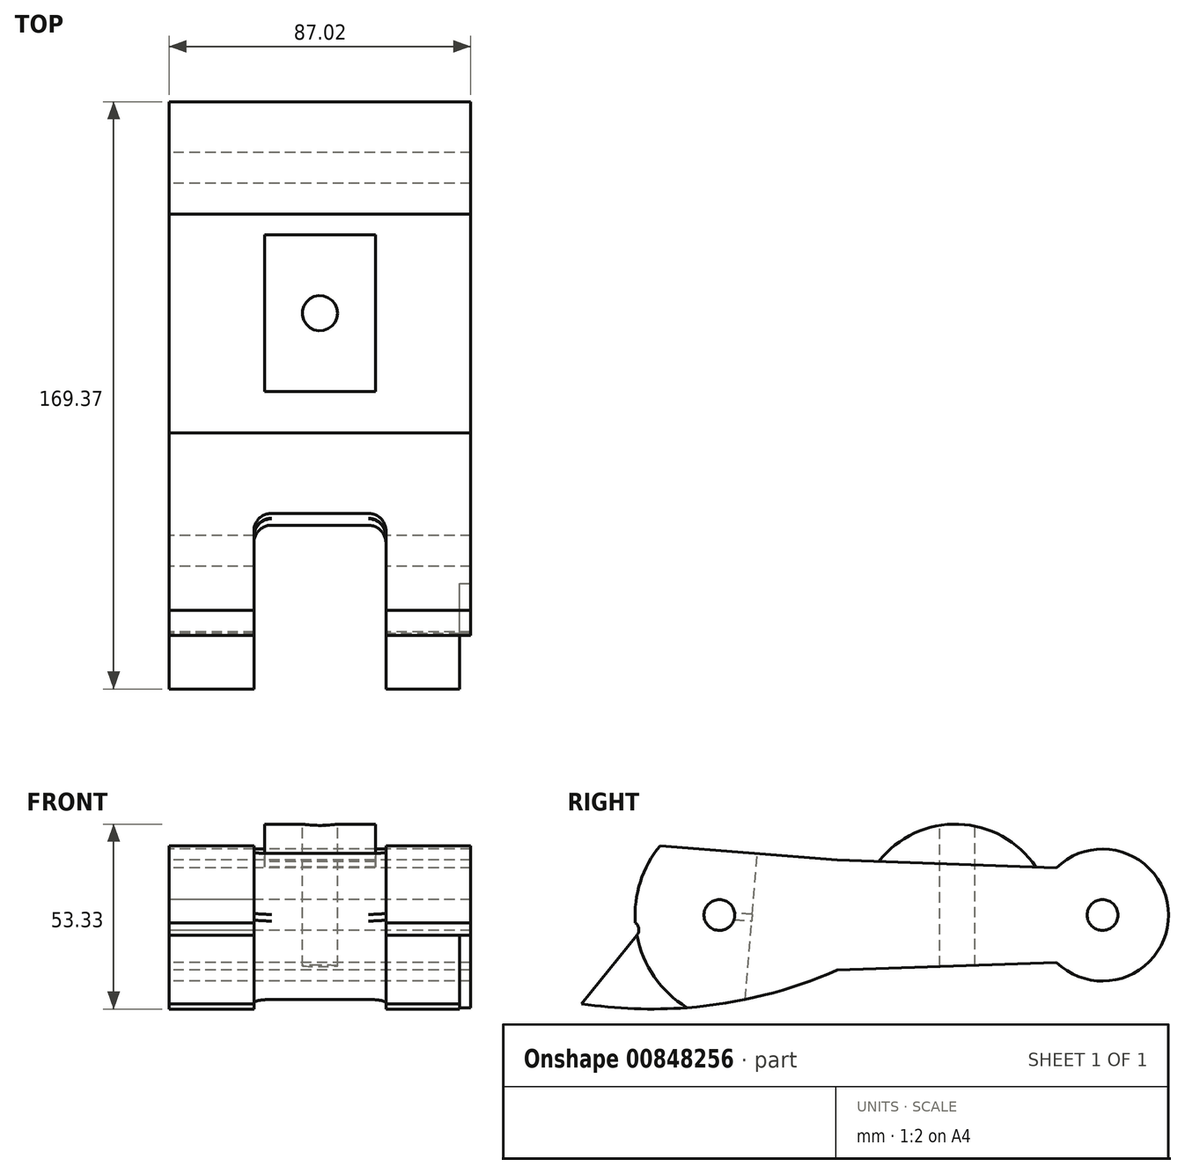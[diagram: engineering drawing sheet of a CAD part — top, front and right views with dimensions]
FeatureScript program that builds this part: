
annotation { "Feature Type Name" : "Feature", "Feature Type Description" : "" }
export const myFeature = defineFeature(function(context is Context, id is Id, definition is map)
    precondition{}
    {
        {
            var Q0;
            Q0=qCreatedBy(makeId("Right.planeOp"),FACE);
            var sketch = newSketch(context, id + "F0", { "sketchPlane" : qUnion([Q0])});
            skArc(sketch, "E0", {"start": v(43.17, -13.65) * mm, "mid": v(75.5, 0) * mm, "end": v(43.17, 13.65) * mm});
            skLineSegment(sketch, "E1", {"start": v(-105.47, 0) * mm, "end": v(-105.47, 71.25) * mm, "construction": true});
            skLineSegment(sketch, "E2", {"start": v(75.5, 0) * mm, "end": v(75.5, 75.21) * mm, "construction": true});
            skLineSegment(sketch, "E3", {"start": v(37.4, 0) * mm, "end": v(37.4, 13.65) * mm, "construction": true});
            skCircle(sketch, "E4", {"center": v(56.46, 0) * mm, "radius": 4.45 * mm});
            skCircle(sketch, "E5", {"center": v(-54.09, 0) * mm, "radius": 4.45 * mm});
            skLineSegment(sketch, "E6", {"start": v(-47.08, -35.85) * mm, "end": v(-47.08, 32.52) * mm, "construction": true});
            skArc(sketch, "E7", {"start": v(-20.04, -15.86) * mm, "mid": v(-15.73, 0) * mm, "end": v(-20.04, 15.86) * mm});
            skPoint(sketch, "E7.centerSnap0", {"position": v(-47.08, -1.67) * mm});
            skLineSegment(sketch, "E8.trimOffspring", {"start": v(-20.04, -15.86) * mm, "end": v(43.17, -13.65) * mm});
            skLineSegment(sketch, "E9.trimOffspring", {"start": v(-20.04, 15.86) * mm, "end": v(43.17, 13.65) * mm});
            skCircle(sketch, "E10", {"center": v(-47.08, 0) * mm, "radius": 31.98 * mm, "construction": true});
            skLineSegment(sketch, "E11", {"start": v(-71.2, 21) * mm, "end": v(-71.2, -21) * mm, "construction": true});
            skLineSegment(sketch, "E12", {"start": v(-78.46, -6.16) * mm, "end": v(-71.2, -21) * mm, "construction": true});
            skLineSegment(sketch, "E13", {"start": v(-78.46, -6.16) * mm, "end": v(-109.55, -44.55) * mm, "construction": true});
            skLineSegment(sketch, "E14", {"start": v(-109.55, -44.55) * mm, "end": v(-71.2, -21) * mm, "construction": true});
            skLineSegment(sketch, "E15.0", {"start": v(-77.87, -5.84) * mm, "end": v(-93.86, -25.58) * mm});
            skLineSegment(sketch, "E16", {"start": v(-93.86, -25.58) * mm, "end": v(-99.5, -21.01) * mm, "construction": true});
            skArc(sketch, "E17", {"start": v(-93.86, -25.58) * mm, "mid": v(-56.26, -25.97) * mm, "end": v(-20.04, -15.86) * mm});
            skLineSegment(sketch, "E18.trimOffspring", {"start": v(-108.9, -44.15) * mm, "end": v(-109.63, -45.05) * mm});
            skLineSegment(sketch, "E19", {"start": v(-71.2, 20.01) * mm, "end": v(-20.04, 15.86) * mm});
            skArc(sketch, "E20.trimOffspring", {"start": v(-71.2, 20.01) * mm, "mid": v(-76.92, 9.6) * mm, "end": v(-78.34, -2.2) * mm});
            skArc(sketch, "E21", {"start": v(-77.87, -5.84) * mm, "mid": v(-77.38, -3.93) * mm, "end": v(-78.34, -2.2) * mm});
            skSolve(sketch);
        }
        {
            var Q0;
            Q0=qSketchRegion(id+"F0",true);
            extrude(context, id + "F1", {"entities" : qUnion([Q0]), "endBound" : BoundingType.SYMMETRIC, "offsetDistance" : 25.4 * mm, "depth" : 87.02 * mm});
        }
        {
            var Q0;
            Q0=makeQuery(id+"F1.opExtrude","SWEPT_FACE",FACE,{"disambiguationData":[OSD([sQuery(id+"F0.wireOp",EDGE,"AqcpRtfy-RzWw-On9u-Weqm-T6a6jaubeQe3")])]});
            var sketch = newSketch(context, id + "F2", { "sketchPlane" : qUnion([Q0])});
            skLineSegment(sketch, "E22.bottom", {"start": v(40.64, -54.4) * mm, "end": v(-40.64, -54.4) * mm});
            skLineSegment(sketch, "E22.top", {"start": v(40.64, -119.07) * mm, "end": v(-40.64, -119.07) * mm});
            skLineSegment(sketch, "E22.left", {"start": v(40.64, -54.4) * mm, "end": v(40.64, -119.07) * mm});
            skLineSegment(sketch, "E22.right", {"start": v(-40.64, -54.4) * mm, "end": v(-40.64, -119.07) * mm});
            skLineSegment(sketch, "E23", {"start": v(0, 0) * mm, "end": v(0, -91.67) * mm, "construction": true});
            skPoint(sketch, "E23.endSnap0", {"position": v(0, -119.07) * mm});
            skSolve(sketch);
        }
        {
            var Q0;
            Q0=qCreatedBy(makeId("Right.planeOp"),FACE);
            var sketch = newSketch(context, id + "F3", { "sketchPlane" : qUnion([Q0])});
            skLineSegment(sketch, "E24.0", {"start": v(-57.66, 17.17) * mm, "end": v(43.17, 13.65) * mm, "construction": true});
            skLineSegment(sketch, "E25", {"start": v(-8.1, 15.44) * mm, "end": v(37.2, 13.86) * mm});
            skArc(sketch, "E26.0", {"start": v(43.17, -13.65) * mm, "mid": v(75.5, 0) * mm, "end": v(43.17, 13.65) * mm, "construction": true});
            skLineSegment(sketch, "E27", {"start": v(75.5, 0) * mm, "end": v(75.5, 55.97) * mm, "construction": true});
            skArc(sketch, "E28", {"start": v(37.2, 13.86) * mm, "mid": v(14.95, 26.2) * mm, "end": v(-8.1, 15.44) * mm});
            skLineSegment(sketch, "E29", {"start": v(14.55, 14.65) * mm, "end": v(14.95, 26.2) * mm, "construction": true});
            skSolve(sketch);
        }
        {
            var Q0;
            Q0=qSketchRegion(id+"F3",true);
            extrude(context, id + "F4", {"entities" : qUnion([Q0]), "operationType" : NewBodyOperationType.ADD, "endBound" : BoundingType.SYMMETRIC, "depth" : 32 * mm});
        }
        {
            var Q0;
            Q0=qCreatedBy(makeId("Top.planeOp"),FACE);
            var sketch = newSketch(context, id + "F5", { "sketchPlane" : qUnion([Q0])});
            skCircle(sketch, "E30", {"center": v(0, 14.55) * mm, "radius": 5.08 * mm});
            skSolve(sketch);
        }
        {
            var Q0;
            Q0=qSketchRegion(id+"F5",true);
            extrude(context, id + "F6", {"entities" : qUnion([Q0]), "operationType" : NewBodyOperationType.REMOVE, "endBound" : BoundingType.SYMMETRIC, "oppositeDirection" : true, "depth" : 152.4 * mm});
        }
        {
            var Q0;
            Q0=makeQuery(id+"F1.opExtrude","CAP_FACE",FACE,{"disambiguationData":[OSD([sQuery(id+"F0.wireOp",EDGE,"E0"),sQuery(id+"F0.wireOp",EDGE,"E4"),sQuery(id+"F0.wireOp",EDGE,"E5"),sQuery(id+"F0.wireOp",EDGE,"E8.trimOffspring"),sQuery(id+"F0.wireOp",EDGE,"E9.trimOffspring"),sQuery(id+"F0.wireOp",EDGE,"E15.0"),sQuery(id+"F0.wireOp",EDGE,"E17"),sQuery(id+"F0.wireOp",EDGE,"E19"),sQuery(id+"F0.wireOp",EDGE,"E20.trimOffspring"),sQuery(id+"F0.wireOp",EDGE,"E21")])],"isStart":false});
            var sketch = newSketch(context, id + "F7", { "sketchPlane" : qUnion([Q0])});
            skArc(sketch, "E31", {"start": v(-77.87, -5.84) * mm, "mid": v(-72.87, -17.8) * mm, "end": v(-63.46, -26.72) * mm});
            skArc(sketch, "E32.0", {"start": v(-93.86, -25.58) * mm, "mid": v(-78.7, -27.02) * mm, "end": v(-63.46, -26.72) * mm});
            skLineSegment(sketch, "E32.1", {"start": v(-77.87, -5.84) * mm, "end": v(-93.86, -25.58) * mm});
            skPoint(sketch, "E33.orphan", {"position": v(-20.04, -15.86) * mm});
            skPoint(sketch, "E34.0.end.orphan", {"position": v(-78.34, -2.2) * mm});
            skPoint(sketch, "E35.orphan", {"position": v(-71.2, 20.01) * mm});
            skSolve(sketch);
        }
        {
            var Q0;
            Q0 = qSketchRegion(id + "F7", true);
            extrude(context, id + "F8", {"entities" : qUnion([Q0]), "operationType" : NewBodyOperationType.REMOVE, "oppositeDirection" : true, "depth" : 3.25 * mm, "offsetDistance" : 25.4 * mm});
        }
        {
            var Q0;
            Q0=makeQuery(id+"F1.opExtrude","SWEPT_FACE",FACE,{"disambiguationData":[OSD([sQuery(id+"F0.wireOp",EDGE,"E19")])]});
            var sketch = newSketch(context, id + "F9", { "sketchPlane" : qUnion([Q0])});
            skLineSegment(sketch, "E36.bottom", {"start": v(19.05, -44.5) * mm, "end": v(-19.05, -44.5) * mm});
            skLineSegment(sketch, "E36.top", {"start": v(19.05, -91.48) * mm, "end": v(-19.05, -91.48) * mm});
            skLineSegment(sketch, "E36.left", {"start": v(19.05, -44.5) * mm, "end": v(19.05, -91.48) * mm});
            skLineSegment(sketch, "E36.right", {"start": v(-19.05, -44.5) * mm, "end": v(-19.05, -91.48) * mm});
            skLineSegment(sketch, "E37", {"start": v(0, 0) * mm, "end": v(0, -88.38) * mm});
            skLineSegment(sketch, "E38.0", {"start": v(40.26, -91.48) * mm, "end": v(-40.26, -91.48) * mm, "construction": true});
            skSolve(sketch);
        }
        {
            var Q0;
            Q0 = qSketchRegion(id + "F9", true);
            extrude(context, id + "F10", {"entities" : qUnion([Q0]), "operationType" : NewBodyOperationType.REMOVE, "endBound" : BoundingType.THROUGH_ALL, "oppositeDirection" : true, "depth" : 25.4 * mm, "offsetDistance" : 25.4 * mm});
        }
        {
            var Q0;
            Q0=makeQuery(id+"F10.boolean.opBoolean","COPY",EDGE,{"derivedFrom":makeQuery(id+"F10.opExtrude","SWEPT_EDGE",EDGE,{"disambiguationData":[OSD([sQuery(id+"F9.wireOp",EDGE,"E36.bottom"),sQuery(id+"F9.wireOp",EDGE,"E36.left")])]})});
            var Q1;
            Q1=makeQuery(id+"F10.boolean.opBoolean","COPY",EDGE,{"derivedFrom":makeQuery(id+"F10.opExtrude","SWEPT_EDGE",EDGE,{"disambiguationData":[OSD([sQuery(id+"F9.wireOp",EDGE,"E36.bottom"),sQuery(id+"F9.wireOp",EDGE,"E36.right")])]})});
            fillet(context, id + "F11", {"entities" : qUnion([Q0, Q1]), "radius" : 5.08 * mm, "tangentPropagation" : true, "allowEdgeOverflow" : false});
        }
    });
